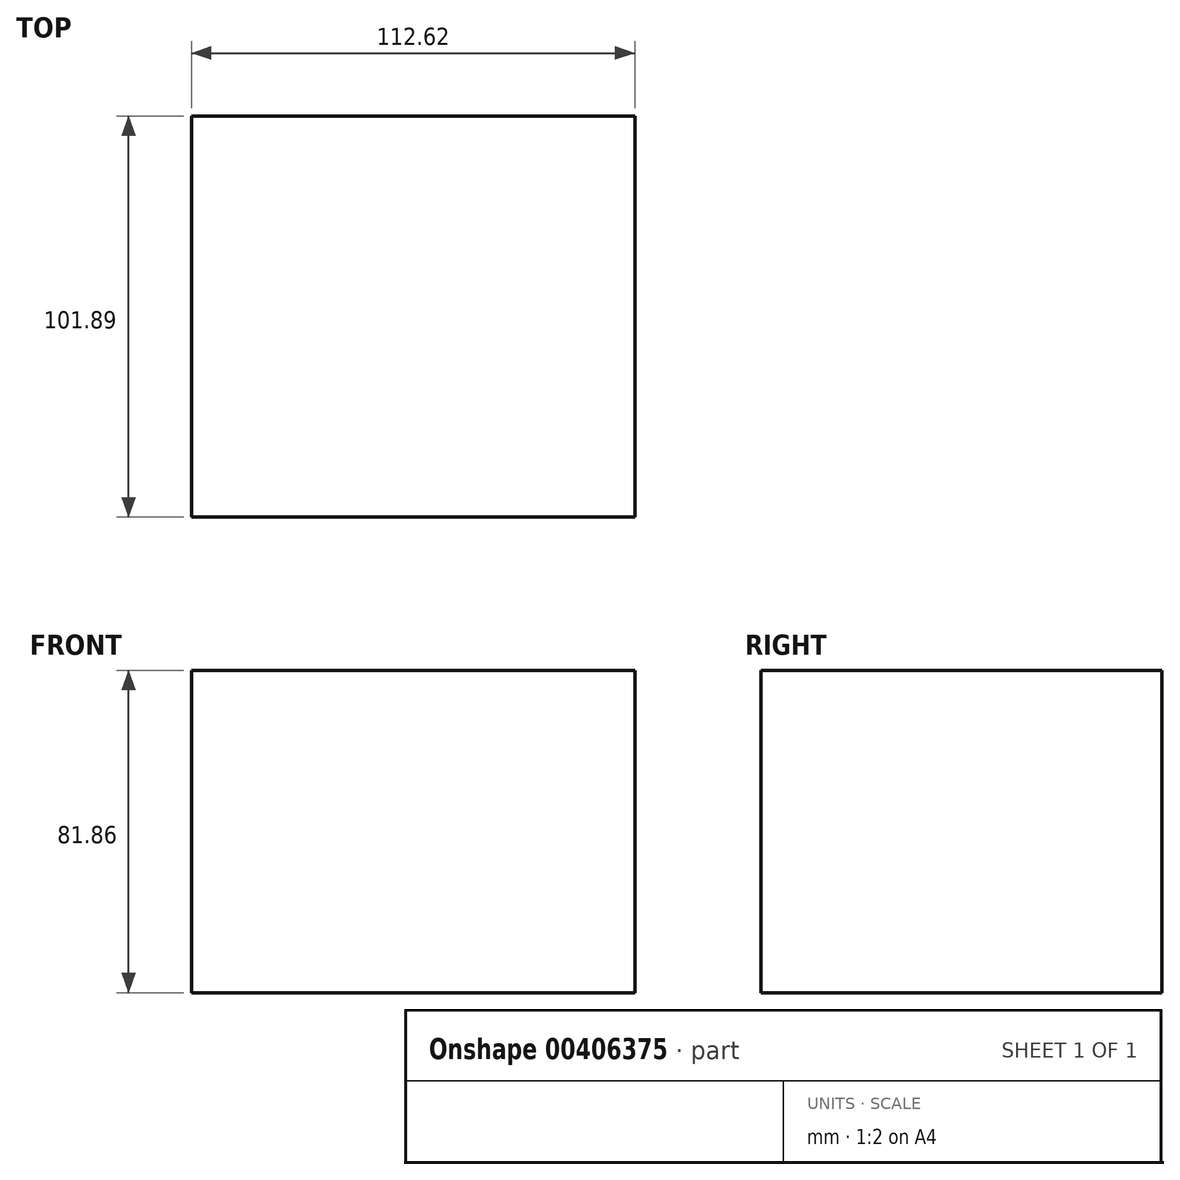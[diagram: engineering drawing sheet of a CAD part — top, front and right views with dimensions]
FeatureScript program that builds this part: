
annotation { "Feature Type Name" : "Feature", "Feature Type Description" : "" }
export const myFeature = defineFeature(function(context is Context, id is Id, definition is map)
    precondition{}
    {
        {
            var Q0;
            Q0=qCreatedBy(makeId("Top.planeOp"),FACE);
            var sketch = newSketch(context, id + "F0", { "sketchPlane" : qUnion([Q0])});
            skLineSegment(sketch, "E0.bottom", {"start": v(59.05, -43.98) * mm, "end": v(-53.57, -43.98) * mm});
            skLineSegment(sketch, "E0.top", {"start": v(59.05, 57.91) * mm, "end": v(-53.57, 57.91) * mm});
            skLineSegment(sketch, "E0.left", {"start": v(59.05, -43.98) * mm, "end": v(59.05, 57.91) * mm});
            skLineSegment(sketch, "E0.right", {"start": v(-53.57, -43.98) * mm, "end": v(-53.57, 57.91) * mm});
            skSolve(sketch);
        }
        {
            var Q0;
            Q0=makeQuery(id+"F0.imprint","IMPRINT",FACE,{"disambiguationData":[TD([[makeQuery(id+"F0.imprint","IMPRINT",EDGE,{"derivedFrom":sQuery(id+"F0.wireOp",EDGE,"E0.bottom")}),-1.0]])]});
            extrude(context, id + "F1", {"entities" : qUnion([Q0]), "depth" : 81.86 * mm});
        }
    });
